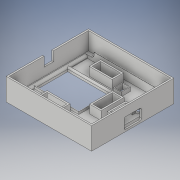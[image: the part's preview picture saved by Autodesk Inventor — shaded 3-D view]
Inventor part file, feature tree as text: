
AUTODESK INVENTOR PART (.ipt)
format: ipt  version: 2019 (Build 230136000, 136)  size: 422,400 bytes
history: native  units: mm
features: extrude x15, sketch x11, fillet x4, mirror x3, other x1, shell x1
ambient origin geometry x8: Origin, YZ Plane, XZ Plane, XY Plane, X Axis, Y Axis, Z Axis, Center Point
bodies: Body1 (feature_tree)
feature tree (35):
  other  "Твердое тело1"
  extrude  "Выдавливание1"  Depth=54.2mm
  shell  "Оболочка1"  Thickness=52.2mm
  extrude  "Выдавливание2"  Depth=14.0mm TaperAngle=0.0deg
  extrude  "Выдавливание3"  Depth=1.0mm
  mirror  "Зеркальное отражение2"
  sketch  "Эскиз4"
  extrude  "Выдавливание4"  Depth=7.5mm
  extrude  "Выдавливание5"  Depth=7.8mm
  mirror  "Зеркальное отражение3"
  extrude  "Выдавливание6"  Depth=3.5mm
  extrude  "Выдавливание7"  Depth=15.0mm TaperAngle=0.0deg
  fillet  "Сопряжение2"  Radius=5.9mm
  extrude  "Выдавливание8"  Depth=5.9mm
  extrude  "Выдавливание12"  Depth=3.5mm
  extrude  "Выдавливание13"  Depth=15.0mm TaperAngle=0.0deg
  mirror  "Зеркальное отражение4"
  fillet  "Сопряжение6"  Radius=17.0mm
  extrude  "Выдавливание14"  Depth=2.5mm
  extrude  "Выдавливание15"  Depth=5.75mm
  extrude  "Выдавливание16"  Depth=9.9mm
  extrude  "Выдавливание18"  Depth=22.1mm
  extrude  "Выдавливание19"  Depth=8.5mm
  fillet  "Сопряжение8"  Radius=15.0mm
  fillet  "Сопряжение9"  Radius=12.6mm
  sketch  "Эскиз1"
  sketch  "Эскиз2"
  sketch  "Эскиз3"
  sketch  "Эскиз5"
  sketch  "Эскиз6"
  sketch  "Эскиз10"
  sketch  "Эскиз11"
  sketch  "Эскиз14"
  sketch  "Эскиз16"
  sketch  "Эскиз17"
